# Revit family: DM_Ворота_Рулонные_Doormaster_EI-60
name_source: partatom
category: Двери
units: mm (PartAtom-declared; Revit-internal decimal feet)

## family parameters
Всегда вертикально = Да
Общий = Нет
Основа = Стена
При загрузке вырезать с полостями = Нет
Точка расчета площади = Нет

## types (1)
- ш.2000 х в.2500
    ADSK_URL страницы изделия = https://www.doormaster.ru
    ADSK_Версия Revit = 2019
    ADSK_Версия семейства = 1
    ADSK_Единица измерения = шт.
    ADSK_Завод-изготовитель = ООО «СТЦ Дормастер»
    ADSK_Код изделия = 20.52.10.190.14.2.02
    ADSK_Количество = 1
    ADSK_Марка = DOORMASTER-FIREPROF-60
    ADSK_Наименование = Противопожарные автоматические рулонные ворота EI-60 2000х2500
    ADSK_Наименование краткое = Противопожарные ворота EI-60 2000х2500
    ADSK_Обозначение = ГОСТ Р 53307-2009
    ADSK_Площадь проемов = 5 м²
    ADSK_Предел огнестойкости = EI-60
    ADSK_Размер_Высота = 2500 мм
    ADSK_Размер_Ширина = 2000 мм
    DM_Диаметр рулона = 730 мм
    H = 3095 мм
    URL = https://www.doormaster.ru
    Высота = 2500 мм
    Изготовитель = ООО «СТЦ Дормастер»
    Направляющие = 2600 мм
    Огнестойкость = EI-60
    Описание = Ворота рулонные (шторы) противопожарные торговой марки «DM-FIREPROF» (предел огнестойкости EI-60) модели «DM-FIREPROF-EI-60» стандартного исполнения (сплошные) или с эвакуационным лазом (выходом), автоматические (с электроприводом) выпускаемые по ТУ 25.12.10−001−63723343−2021 из кремнеземной ткани типа КТ-1-660, ТУ-13.96.14-011-99176106-2018, толщиной не менее 0,6 мм, плотностью не менее 600г/м² и внутреннего слоя из иглопрошивного мата типа CF-500-3 плотностью не менее 500г/м², общей толщиной полотна не менее 10 мм, прошитое кремнеземной нитью типа К11С6-250-БА(230)-ОТ, ТУ 5952-191-05786904-2007, и конструктивными элементами корпуса из стали (толщина стали профилей направляющих и подвижной планки не менее 1,5 мм), выпускаемые по ТУ 25.12.10-001-63723343-2021
    Ось = 425 мм
    Тип конструкций = Ворота рулонные противопожарные
    Толщина = 65 мм
    Толщина направляющей = 120 мм
    Функция = Наружные слои
    Ширина = 2000 мм
    Ширина направляющей = 120 мм
